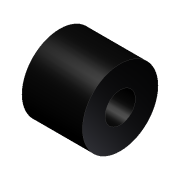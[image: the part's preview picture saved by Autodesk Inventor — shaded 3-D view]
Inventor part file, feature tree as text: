
AUTODESK INVENTOR PART (.ipt)
format: ipt  version: 2012 (Build 160160000, 160)  size: 82,944 bytes
history: native  units: in
note: dims shown in document units (in); Inventor stores cm internally (conversion verified against a paired STEP export)
features: extrude x1, sketch x1
ambient origin geometry x8: Origin, YZ Plane, XZ Plane, XY Plane, X Axis, Y Axis, Z Axis, Center Point
bodies: Solid1 (feature_tree)
feature tree (2):
  extrude  "Extrusion1"  Depth=0.625in
  sketch  "Sketch1"  dims[d0=0.251in d1=0.625in d2=0.5in d3=0.0in]
